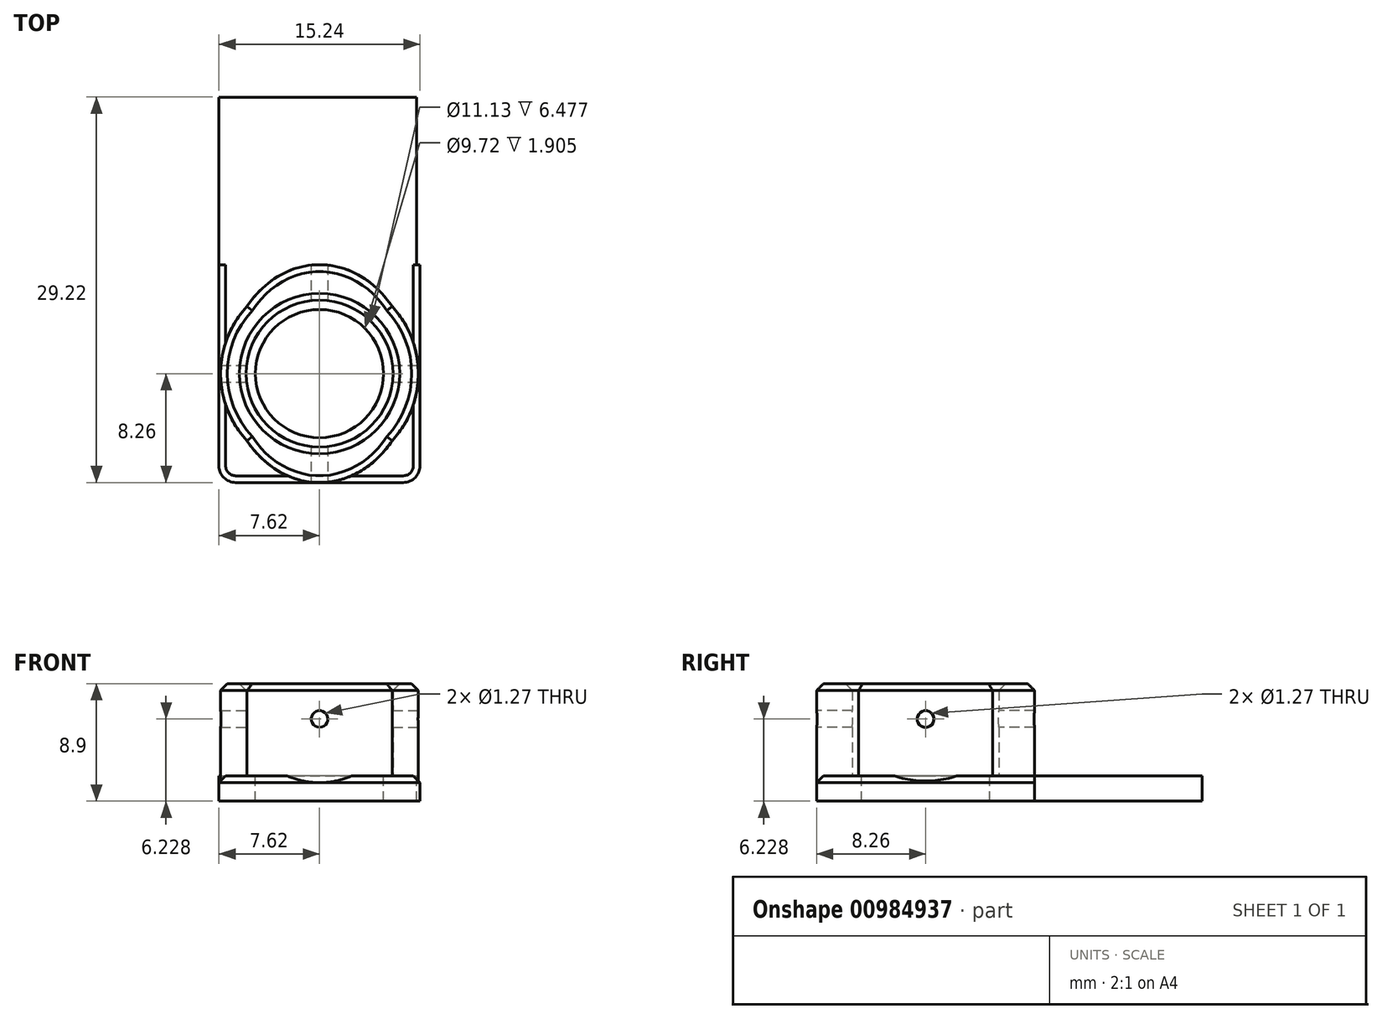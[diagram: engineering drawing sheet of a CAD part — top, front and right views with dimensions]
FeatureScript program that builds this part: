
annotation { "Feature Type Name" : "Feature", "Feature Type Description" : "" }
export const myFeature = defineFeature(function(context is Context, id is Id, definition is map)
    precondition{}
    {
        {
            var Q0;
            Q0=qCreatedBy(makeId("Top.planeOp"),FACE);
            var sketch = newSketch(context, id + "F0", { "sketchPlane" : qUnion([Q0])});
            skPoint(sketch, "E0.middle", {"position": v(0, 0) * mm});
            skCircle(sketch, "E1", {"center": v(0, 0) * mm, "radius": 7.5 * mm});
            skCircle(sketch, "E2", {"center": v(0, 0) * mm, "radius": 5.56 * mm});
            skEllipse(sketch, "E3", {"center": v(0, 0) * mm, "majorRadius": 8.26 * mm, "minorRadius": 6.99 * mm, "majorAxis": v(0, 1)});
            skSolve(sketch);
        }
        {
            var Q0;
            Q0=makeQuery(id+"F0.imprint","IMPRINT",FACE,{"disambiguationData":[TD([[makeQuery(id+"F0.imprint","IMPRINT",EDGE,{"derivedFrom":sQuery(id+"F0.wireOp",EDGE,"E1")}),1.0]])]});
            var Q1;
            {var subQ0=sQuery(id+"F0.wireOp",EDGE,"E3");var subQ1=sQuery(id+"F0.wireOp",EDGE,"E1");var subQ2=makeQuery(id+"F0.imprint","INTERSECT",VERTEX,{"disambiguationData":[OD(0.0)],"derivedFrom":[subQ1,subQ0]});Q1=makeQuery(id+"F0.imprint","IMPRINT",FACE,{"disambiguationData":[TD([[makeQuery(id+"F0.imprint","IMPRINT",EDGE,{"disambiguationData":[TD([[subQ2,1.0]])],"derivedFrom":subQ1}),-1.0]])]});}
            var Q2;
            {var subQ0=sQuery(id+"F0.wireOp",EDGE,"E3");var subQ1=sQuery(id+"F0.wireOp",EDGE,"E1");var subQ2=makeQuery(id+"F0.imprint","INTERSECT",VERTEX,{"disambiguationData":[OD(2.0)],"derivedFrom":[subQ1,subQ0]});Q2=makeQuery(id+"F0.imprint","IMPRINT",FACE,{"disambiguationData":[TD([[makeQuery(id+"F0.imprint","IMPRINT",EDGE,{"disambiguationData":[TD([[subQ2,-1.0]])],"derivedFrom":subQ1}),-1.0]])]});}
            var Q3;
            {var subQ0=sQuery(id+"F0.wireOp",EDGE,"E3");var subQ1=sQuery(id+"F0.wireOp",EDGE,"E1");var subQ2=makeQuery(id+"F0.imprint","INTERSECT",VERTEX,{"disambiguationData":[OD(0.0)],"derivedFrom":[subQ1,subQ0]});Q3=makeQuery(id+"F0.imprint","IMPRINT",FACE,{"disambiguationData":[TD([[makeQuery(id+"F0.imprint","IMPRINT",EDGE,{"disambiguationData":[TD([[subQ2,-1.0]])],"derivedFrom":subQ1}),1.0]])]});}
            var Q4;
            {var subQ0=sQuery(id+"F0.wireOp",EDGE,"E3");var subQ1=sQuery(id+"F0.wireOp",EDGE,"E1");var subQ2=makeQuery(id+"F0.imprint","INTERSECT",VERTEX,{"disambiguationData":[OD(1.0)],"derivedFrom":[subQ1,subQ0]});Q4=makeQuery(id+"F0.imprint","IMPRINT",FACE,{"disambiguationData":[TD([[makeQuery(id+"F0.imprint","IMPRINT",EDGE,{"disambiguationData":[TD([[subQ2,1.0]])],"derivedFrom":subQ1}),1.0]])]});}
            extrude(context, id + "F1", {"entities" : qUnion([Q0, Q1, Q2, Q3, Q4]), "depth" : 7 * mm, "offsetDistance" : 25.4 * mm});
        }
        {
            var Q0;
            Q0=qCreatedBy(makeId("Right.planeOp"),FACE);
            var sketch = newSketch(context, id + "F2", { "sketchPlane" : qUnion([Q0])});
            skCircle(sketch, "E4", {"center": v(0, 4.32) * mm, "radius": 0.64 * mm});
            skSolve(sketch);
        }
        {
            var Q0;
            Q0=makeQuery(id+"F2.imprint","IMPRINT",FACE,{"disambiguationData":[TD([[makeQuery(id+"F2.imprint","IMPRINT",EDGE,{"derivedFrom":sQuery(id+"F2.wireOp",EDGE,"E4")}),1.0]])]});
            extrude(context, id + "F3", {"entities" : qUnion([Q0]), "operationType" : NewBodyOperationType.REMOVE, "endBound" : BoundingType.SYMMETRIC, "oppositeDirection" : true, "depth" : 50.8 * mm, "offsetDistance" : 25.4 * mm});
        }
        {
            var Q0;
            Q0=qCreatedBy(makeId("Front.planeOp"),FACE);
            var sketch = newSketch(context, id + "F4", { "sketchPlane" : qUnion([Q0])});
            skCircle(sketch, "E5", {"center": v(0, 4.32) * mm, "radius": 0.64 * mm});
            skSolve(sketch);
        }
        {
            var Q0;
            Q0=qCreatedBy(makeId("Top.planeOp"),FACE);
            var sketch = newSketch(context, id + "F5", { "sketchPlane" : qUnion([Q0])});
            skLineSegment(sketch, "E6.bottom", {"start": v(7.62, 8.26) * mm, "end": v(-7.62, 8.26) * mm});
            skLineSegment(sketch, "E6.top", {"start": v(7.62, -8.26) * mm, "end": v(-7.62, -8.26) * mm});
            skLineSegment(sketch, "E6.left", {"start": v(7.62, 8.26) * mm, "end": v(7.62, -8.26) * mm});
            skLineSegment(sketch, "E6.right", {"start": v(-7.62, 8.26) * mm, "end": v(-7.62, -8.26) * mm});
            skPoint(sketch, "E6.middle", {"position": v(0, 0) * mm});
            skSolve(sketch);
        }
        {
            var Q0;
            Q0=makeQuery(id+"F5.imprint","IMPRINT",FACE,{"disambiguationData":[TD([[makeQuery(id+"F5.imprint","IMPRINT",EDGE,{"derivedFrom":sQuery(id+"F5.wireOp",EDGE,"E6.bottom")}),1.0]])]});
            extrude(context, id + "F6", {"entities" : qUnion([Q0]), "operationType" : NewBodyOperationType.ADD, "oppositeDirection" : true, "depth" : 1.9 * mm, "offsetDistance" : 25.4 * mm});
        }
        {
            var Q0;
            {var subQ0=sQuery(id+"F5.wireOp",EDGE,"E6.left");var subQ1=sQuery(id+"F5.wireOp",EDGE,"E6.bottom");var subQ2=sQuery(id+"F5.wireOp",EDGE,"E6.top");var subQ3=sQuery(id+"F5.wireOp",EDGE,"E6.right");Q0=makeQuery(id+"F6.boolean.opBoolean","SPLIT",FACE,{"disambiguationData":[TD([makeQuery(id+"F1.opExtrude","SWEPT_FACE",FACE,{"disambiguationData":[OSD([sQuery(id+"F0.wireOp",EDGE,"E1")])]})])],"derivedFrom":makeQuery(id+"F6.opExtrude","CAP_FACE",FACE,{"disambiguationData":[OSD([subQ1,subQ2,subQ0,subQ3])],"isStart":true})});}
            var sketch = newSketch(context, id + "F7", { "sketchPlane" : qUnion([Q0])});
            skCircle(sketch, "E7", {"center": v(0, 0) * mm, "radius": 4.86 * mm});
            skSolve(sketch);
        }
        {
            var Q0;
            Q0=makeQuery(id+"F7.imprint","IMPRINT",FACE,{"disambiguationData":[TD([[makeQuery(id+"F7.imprint","IMPRINT",EDGE,{"derivedFrom":sQuery(id+"F7.wireOp",EDGE,"E7")}),1.0]])]});
            extrude(context, id + "F8", {"entities" : qUnion([Q0]), "operationType" : NewBodyOperationType.REMOVE, "oppositeDirection" : true, "depth" : 2.54 * mm, "offsetDistance" : 25.4 * mm});
        }
        {
            var Q0;
            Q0=makeQuery(id+"F6.opExtrude","SWEPT_EDGE",EDGE,{"disambiguationData":[OSD([sQuery(id+"F5.wireOp",EDGE,"E6.top"),sQuery(id+"F5.wireOp",EDGE,"E6.right")])]});
            var Q1;
            Q1=makeQuery(id+"F6.opExtrude","SWEPT_EDGE",EDGE,{"disambiguationData":[OSD([sQuery(id+"F5.wireOp",EDGE,"E6.top"),sQuery(id+"F5.wireOp",EDGE,"E6.left")])]});
            fillet(context, id + "F9", {"entities" : qUnion([Q0, Q1]), "radius" : 1.27 * mm, "tangentPropagation" : true, "allowEdgeOverflow" : false});
        }
        {
            var Q0;
            {var subQ0=sQuery(id+"F0.wireOp",EDGE,"E3");var subQ1=sQuery(id+"F0.wireOp",EDGE,"E1");Q0=makeQuery(id+"F1.opExtrude","CAP_EDGE",EDGE,{"disambiguationData":[OSD([subQ0]),TDD([makeQuery(id+"F0.imprint","IMPRINT",EDGE,{"disambiguationData":[TD([[makeQuery(id+"F0.imprint","INTERSECT",VERTEX,{"disambiguationData":[OD(2.0)],"derivedFrom":[subQ1,subQ0]}),-1.0]])],"derivedFrom":subQ0})])],"isStart":false});}
            var Q1;
            {var subQ0=sQuery(id+"F0.wireOp",EDGE,"E3");var subQ1=sQuery(id+"F0.wireOp",EDGE,"E1");Q1=makeQuery(id+"F1.opExtrude","CAP_EDGE",EDGE,{"disambiguationData":[OSD([subQ0]),TDD([makeQuery(id+"F0.imprint","IMPRINT",EDGE,{"disambiguationData":[TD([[makeQuery(id+"F0.imprint","INTERSECT",VERTEX,{"disambiguationData":[OD(0.0)],"derivedFrom":[subQ1,subQ0]}),1.0]])],"derivedFrom":subQ0})])],"isStart":false});}
            var Q2;
            {var subQ0=sQuery(id+"F0.wireOp",EDGE,"E3");var subQ1=sQuery(id+"F0.wireOp",EDGE,"E1");Q2=makeQuery(id+"F1.opExtrude","CAP_EDGE",EDGE,{"disambiguationData":[OSD([subQ1]),TDD([makeQuery(id+"F0.imprint","IMPRINT",EDGE,{"disambiguationData":[TD([[makeQuery(id+"F0.imprint","INTERSECT",VERTEX,{"disambiguationData":[OD(1.0)],"derivedFrom":[subQ1,subQ0]}),1.0]])],"derivedFrom":subQ1})])],"isStart":false});}
            var Q3;
            {var subQ0=sQuery(id+"F0.wireOp",EDGE,"E3");var subQ1=sQuery(id+"F0.wireOp",EDGE,"E1");Q3=makeQuery(id+"F1.opExtrude","CAP_EDGE",EDGE,{"disambiguationData":[OSD([subQ1]),TDD([makeQuery(id+"F0.imprint","IMPRINT",EDGE,{"disambiguationData":[TD([[makeQuery(id+"F0.imprint","INTERSECT",VERTEX,{"disambiguationData":[OD(0.0)],"derivedFrom":[subQ1,subQ0]}),-1.0]])],"derivedFrom":subQ1})])],"isStart":false});}
            var Q4;
            Q4=makeQuery(id+"F1.opExtrude","CAP_EDGE",EDGE,{"disambiguationData":[OSD([sQuery(id+"F0.wireOp",EDGE,"E2")])],"isStart":false});
            var Q5;
            Q5=makeQuery(id+"F6.opExtrude","CAP_EDGE",EDGE,{"disambiguationData":[OSD([sQuery(id+"F5.wireOp",EDGE,"E6.left")])],"isStart":true});
            chamfer(context, id + "F10", {"entities" : qUnion([Q0, Q1, Q2, Q3, Q4, Q5]), "width" : 0.5 * mm, "tangentPropagation" : true});
        }
        {
            var Q0;
            Q0=makeQuery(id+"F4.imprint","IMPRINT",FACE,{"disambiguationData":[TD([[makeQuery(id+"F4.imprint","IMPRINT",EDGE,{"derivedFrom":sQuery(id+"F4.wireOp",EDGE,"E5")}),1.0]])]});
            extrude(context, id + "F11", {"entities" : qUnion([Q0]), "operationType" : NewBodyOperationType.REMOVE, "endBound" : BoundingType.SYMMETRIC, "oppositeDirection" : true, "depth" : 25.4 * mm, "offsetDistance" : 25.4 * mm});
        }
        {
            var Q0;
            Q0=makeQuery(id+"F6.opExtrude","SWEPT_FACE",FACE,{"disambiguationData":[OSD([sQuery(id+"F5.wireOp",EDGE,"E6.bottom")])]});
            var sketch = newSketch(context, id + "F12", { "sketchPlane" : qUnion([Q0])});
            skPoint(sketch, "E8.oppositeSnap0", {"position": v(-7.37, -0.25) * mm});
            skLineSegment(sketch, "E8.bottom", {"start": v(7.62, -1.9) * mm, "end": v(-7.37, -1.9) * mm});
            skLineSegment(sketch, "E8.top", {"start": v(7.62, 0) * mm, "end": v(-7.37, 0) * mm});
            skLineSegment(sketch, "E8.left", {"start": v(7.62, -1.9) * mm, "end": v(7.62, 0) * mm});
            skLineSegment(sketch, "E8.right", {"start": v(-7.37, -1.9) * mm, "end": v(-7.37, 0) * mm});
            skSolve(sketch);
        }
        {
            var Q0;
            Q0 = qSketchRegion(id + "F12", true);
            extrude(context, id + "F13", {"entities" : qUnion([Q0]), "operationType" : NewBodyOperationType.ADD, "depth" : 12.7 * mm, "offsetDistance" : 25.4 * mm});
        }
    });
